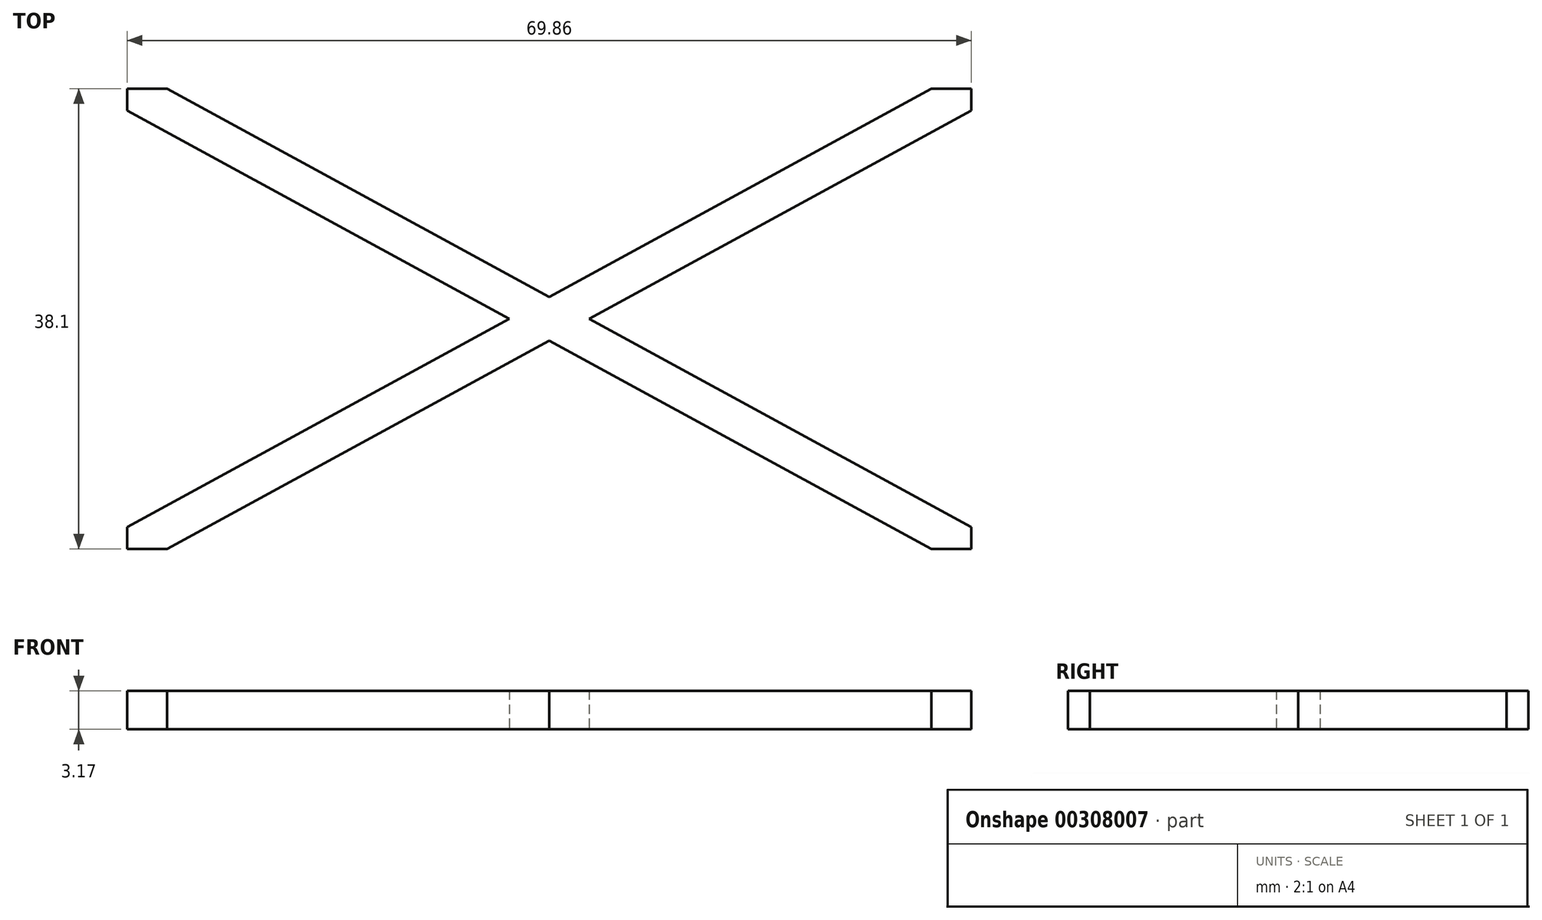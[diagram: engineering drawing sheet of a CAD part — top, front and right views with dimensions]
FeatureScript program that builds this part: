
annotation { "Feature Type Name" : "Feature", "Feature Type Description" : "" }
export const myFeature = defineFeature(function(context is Context, id is Id, definition is map)
    precondition{}
    {
        {
            var Q0;
            Q0=qCreatedBy(makeId("Top.planeOp"),FACE);
            var sketch = newSketch(context, id + "F0", { "sketchPlane" : qUnion([Q0])});
            skLineSegment(sketch, "E0", {"start": v(-34.93, -19.05) * mm, "end": v(34.93, 19.05) * mm, "construction": true});
            skLineSegment(sketch, "E1", {"start": v(34.93, -19.05) * mm, "end": v(-34.93, 19.05) * mm, "construction": true});
            skLineSegment(sketch, "E2.0", {"start": v(-31.6, -19.05) * mm, "end": v(34.92, 17.24) * mm});
            skLineSegment(sketch, "E3.0", {"start": v(-34.93, -17.24) * mm, "end": v(31.15, 18.8) * mm});
            skLineSegment(sketch, "E4.0", {"start": v(34.92, -17.24) * mm, "end": v(-31.6, 19.05) * mm});
            skLineSegment(sketch, "E5.0", {"start": v(31.15, -18.8) * mm, "end": v(-34.93, 17.24) * mm});
            skLineSegment(sketch, "E6", {"start": v(-34.93, 19.05) * mm, "end": v(-34.93, 17.24) * mm});
            skLineSegment(sketch, "E7", {"start": v(-34.93, -17.24) * mm, "end": v(-34.93, -19.05) * mm});
            skLineSegment(sketch, "E8", {"start": v(34.92, 17.24) * mm, "end": v(34.93, 19.05) * mm});
            skLineSegment(sketch, "E9", {"start": v(34.92, -17.24) * mm, "end": v(34.93, -19.05) * mm});
            skPoint(sketch, "E10", {"position": v(0, 0) * mm});
            skLineSegment(sketch, "E11", {"start": v(0, 0) * mm, "end": v(0, 1.8) * mm, "construction": true});
            skLineSegment(sketch, "E12", {"start": v(0, 1.8) * mm, "end": v(0, -1.8) * mm, "construction": true});
            skLineSegment(sketch, "E13", {"start": v(-34.93, 19.05) * mm, "end": v(-31.6, 19.05) * mm});
            skLineSegment(sketch, "E14", {"start": v(31.15, 18.8) * mm, "end": v(31.6, 19.05) * mm});
            skLineSegment(sketch, "E15.trimOffspring", {"start": v(31.6, 19.05) * mm, "end": v(34.93, 19.05) * mm});
            skLineSegment(sketch, "E16", {"start": v(-34.93, -19.05) * mm, "end": v(-31.6, -19.05) * mm});
            skLineSegment(sketch, "E17", {"start": v(31.15, -18.8) * mm, "end": v(31.6, -19.05) * mm});
            skLineSegment(sketch, "E18.trimOffspring", {"start": v(31.6, -19.05) * mm, "end": v(34.93, -19.05) * mm});
            skSolve(sketch);
        }
        {
            var Q0;
            {var subQ0=sQuery(id+"F0.wireOp",EDGE,"E8");Q0=makeQuery(id+"F0.imprint","IMPRINT",FACE,{"disambiguationData":[TD([[makeQuery(id+"F0.imprint","IMPRINT",EDGE,{"derivedFrom":subQ0}),1.0]])]});}
            var Q1;
            {var subQ0=sQuery(id+"F0.wireOp",EDGE,"E7");Q1=makeQuery(id+"F0.imprint","IMPRINT",FACE,{"disambiguationData":[TD([[makeQuery(id+"F0.imprint","IMPRINT",EDGE,{"derivedFrom":subQ0}),1.0]])]});}
            var Q2;
            {var subQ0=sQuery(id+"F0.wireOp",EDGE,"E6");Q2=makeQuery(id+"F0.imprint","IMPRINT",FACE,{"disambiguationData":[TD([[makeQuery(id+"F0.imprint","IMPRINT",EDGE,{"derivedFrom":subQ0}),1.0]])]});}
            var Q3;
            {var subQ0=sQuery(id+"F0.wireOp",EDGE,"E9");Q3=makeQuery(id+"F0.imprint","IMPRINT",FACE,{"disambiguationData":[TD([[makeQuery(id+"F0.imprint","IMPRINT",EDGE,{"derivedFrom":subQ0}),-1.0]])]});}
            var Q4;
            {var subQ0=sQuery(id+"F0.wireOp",EDGE,"E5.0");var subQ1=sQuery(id+"F0.wireOp",EDGE,"E2.0");var subQ2=makeQuery(id+"F0.imprint","INTERSECT",VERTEX,{"derivedFrom":[subQ1,subQ0]});Q4=makeQuery(id+"F0.imprint","IMPRINT",FACE,{"disambiguationData":[TD([[makeQuery(id+"F0.imprint","IMPRINT",EDGE,{"disambiguationData":[TD([[subQ2,-1.0]])],"derivedFrom":subQ1}),1.0]])]});}
            extrude(context, id + "F1", {"entities" : qUnion([Q0, Q1, Q2, Q3, Q4]), "depth" : 3.17 * mm});
        }
    });
